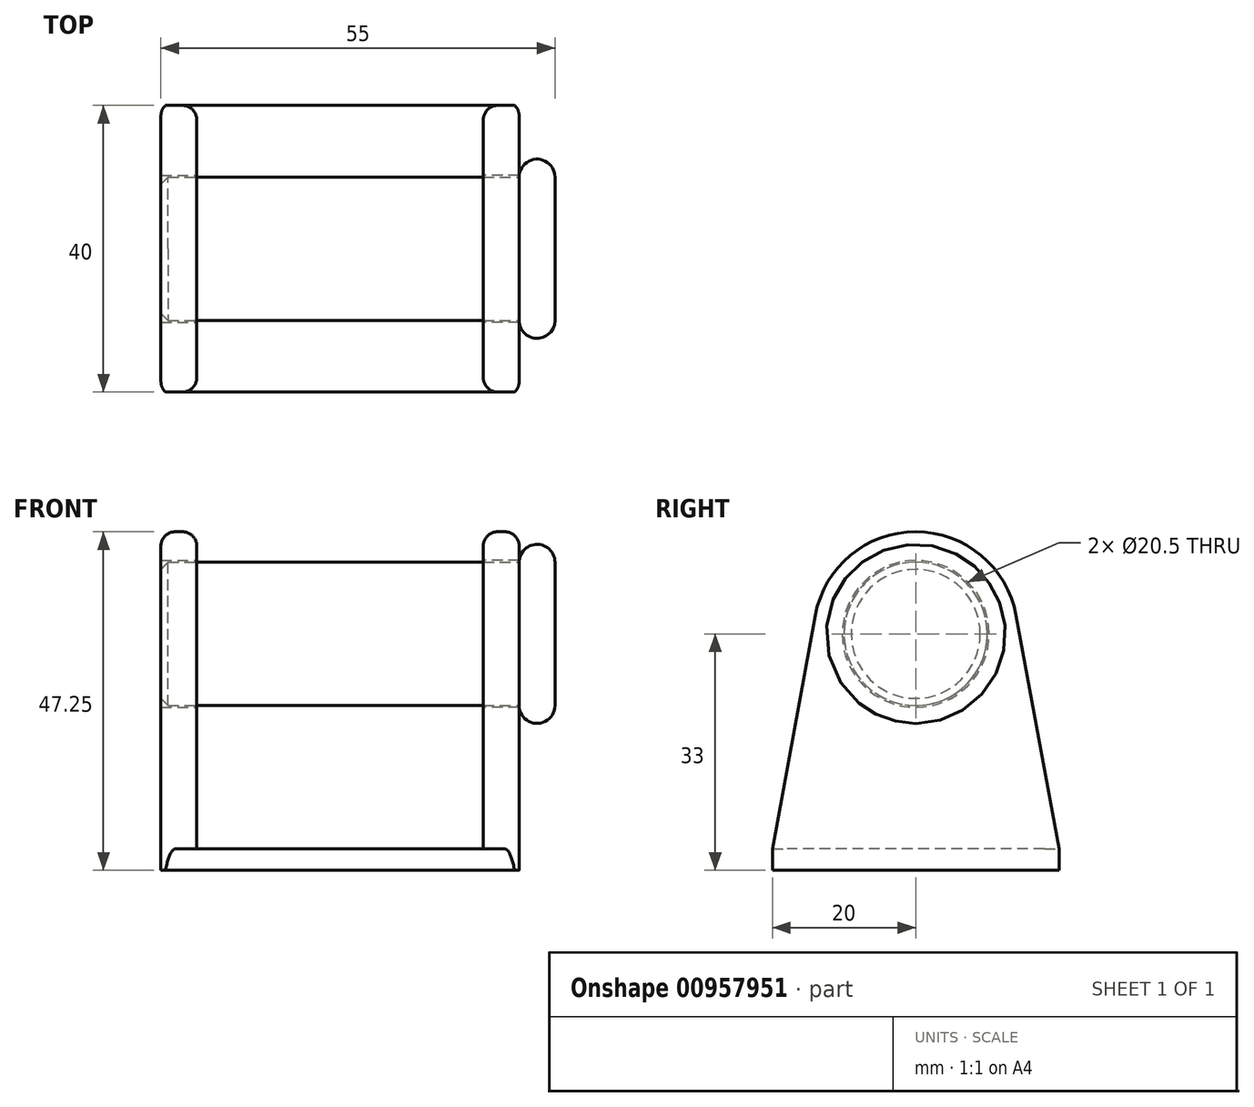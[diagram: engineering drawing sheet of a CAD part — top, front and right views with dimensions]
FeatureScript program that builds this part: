
annotation { "Feature Type Name" : "Feature", "Feature Type Description" : "" }
export const myFeature = defineFeature(function(context is Context, id is Id, definition is map)
    precondition{}
    {
        {
            var Q0;
            Q0=qCreatedBy(makeId("Top.planeOp"),FACE);
            var sketch = newSketch(context, id + "F0", { "sketchPlane" : qUnion([Q0])});
            skLineSegment(sketch, "E0.bottom", {"start": v(25, 20) * mm, "end": v(-25, 20) * mm});
            skLineSegment(sketch, "E0.top", {"start": v(25, -20) * mm, "end": v(-25, -20) * mm});
            skLineSegment(sketch, "E0.left", {"start": v(25, 20) * mm, "end": v(25, -20) * mm});
            skLineSegment(sketch, "E0.right", {"start": v(-25, 20) * mm, "end": v(-25, -20) * mm});
            skPoint(sketch, "E0.middle", {"position": v(0, 0) * mm});
            skLineSegment(sketch, "E1.bottom", {"start": v(20, 20) * mm, "end": v(-20, 20) * mm});
            skLineSegment(sketch, "E1.top", {"start": v(20, -20) * mm, "end": v(-20, -20) * mm});
            skLineSegment(sketch, "E1.left", {"start": v(20, 20) * mm, "end": v(20, -20) * mm});
            skLineSegment(sketch, "E1.right", {"start": v(-20, 20) * mm, "end": v(-20, -20) * mm});
            skSolve(sketch);
        }
        {
            var Q0;
            {var subQ0=sQuery(id+"F0.wireOp",EDGE,"E1.left");Q0=makeQuery(id+"F0.imprint","IMPRINT",FACE,{"disambiguationData":[TD([[makeQuery(id+"F0.imprint","IMPRINT",EDGE,{"derivedFrom":subQ0}),-1.0]])]});}
            var Q1;
            {var subQ0=sQuery(id+"F0.wireOp",EDGE,"E0.right");Q1=makeQuery(id+"F0.imprint","IMPRINT",FACE,{"disambiguationData":[TD([[makeQuery(id+"F0.imprint","IMPRINT",EDGE,{"derivedFrom":subQ0}),1.0]])]});}
            var Q2;
            {var subQ2=sQuery(id+"F0.wireOp",EDGE,"E0.left");Q2=makeQuery(id+"F0.imprint","IMPRINT",FACE,{"disambiguationData":[TD([[makeQuery(id+"F0.imprint","IMPRINT",EDGE,{"derivedFrom":subQ2}),-1.0]])]});}
            extrude(context, id + "F1", {"entities" : qUnion([Q0, Q1, Q2]), "depth" : 3 * mm, "offsetDistance" : 25 * mm});
        }
        {
            var Q0;
            Q0=qCreatedBy(makeId("Right.planeOp"),FACE);
            var sketch = newSketch(context, id + "F2", { "sketchPlane" : qUnion([Q0])});
            skCircle(sketch, "E2", {"center": v(0, 33) * mm, "radius": 10.25 * mm});
            skCircle(sketch, "E3", {"center": v(0, 33) * mm, "radius": 14.25 * mm});
            skLineSegment(sketch, "E4.0", {"start": v(20, 3) * mm, "end": v(-20, 3) * mm});
            skLineSegment(sketch, "E5", {"start": v(-20, 3) * mm, "end": v(-14.02, 35.57) * mm});
            skLineSegment(sketch, "E6", {"start": v(20, 3) * mm, "end": v(14.02, 35.57) * mm});
            skSolve(sketch);
        }
        {
            var Q0;
            Q0=makeQuery(id+"F2.imprint","IMPRINT",FACE,{"disambiguationData":[TD([[makeQuery(id+"F2.imprint","IMPRINT",EDGE,{"derivedFrom":sQuery(id+"F2.wireOp",EDGE,"E4.0")}),-1.0]])]});
            var Q1;
            Q1=makeQuery(id+"F2.imprint","IMPRINT",FACE,{"disambiguationData":[TD([[makeQuery(id+"F2.imprint","IMPRINT",EDGE,{"derivedFrom":sQuery(id+"F2.wireOp",EDGE,"E2")}),-1.0]])]});
            extrude(context, id + "F3", {"entities" : qUnion([Q0, Q1]), "operationType" : NewBodyOperationType.ADD, "depth" : 25 * mm, "offsetDistance" : 25 * mm, "hasSecondDirection" : true, "secondDirectionOppositeDirection" : false, "secondDirectionDepth" : 20 * mm});
        }
        {
            var Q0;
            Q0=makeQuery(id+"F2.imprint","IMPRINT",FACE,{"disambiguationData":[TD([[makeQuery(id+"F2.imprint","IMPRINT",EDGE,{"derivedFrom":sQuery(id+"F2.wireOp",EDGE,"E4.0")}),-1.0]])]});
            var Q1;
            Q1=makeQuery(id+"F2.imprint","IMPRINT",FACE,{"disambiguationData":[TD([[makeQuery(id+"F2.imprint","IMPRINT",EDGE,{"derivedFrom":sQuery(id+"F2.wireOp",EDGE,"E2")}),-1.0]])]});
            extrude(context, id + "F4", {"entities" : qUnion([Q0, Q1]), "operationType" : NewBodyOperationType.ADD, "oppositeDirection" : true, "depth" : 25 * mm, "offsetDistance" : 25 * mm, "hasSecondDirection" : true, "secondDirectionOppositeDirection" : true, "secondDirectionDepth" : 20 * mm});
        }
        {
            var Q0;
            Q0=qCreatedBy(makeId("Front.planeOp"),FACE);
            var sketch = newSketch(context, id + "F5", { "sketchPlane" : qUnion([Q0])});
            skPoint(sketch, "E7.0", {"position": v(0, 33) * mm});
            skLineSegment(sketch, "E8.bottom", {"start": v(25, 23) * mm, "end": v(-25, 23) * mm});
            skLineSegment(sketch, "E8.top", {"start": v(25, 43) * mm, "end": v(-25, 43) * mm});
            skLineSegment(sketch, "E8.left", {"start": v(25, 23) * mm, "end": v(25, 43) * mm});
            skLineSegment(sketch, "E8.right", {"start": v(-25, 23) * mm, "end": v(-25, 43) * mm});
            skLineSegment(sketch, "E9", {"start": v(25, 33) * mm, "end": v(-25, 33) * mm});
            skLineSegment(sketch, "E10.bottom", {"start": v(25, 45.5) * mm, "end": v(30, 45.5) * mm});
            skLineSegment(sketch, "E10.top", {"start": v(25, 20.5) * mm, "end": v(30, 20.5) * mm});
            skLineSegment(sketch, "E10.left", {"start": v(25, 45.5) * mm, "end": v(25, 20.5) * mm});
            skLineSegment(sketch, "E10.right", {"start": v(30, 45.5) * mm, "end": v(30, 20.5) * mm});
            skPoint(sketch, "E10.middle", {"position": v(27.5, 33) * mm});
            skLineSegment(sketch, "E11", {"start": v(25, 33) * mm, "end": v(30, 33) * mm});
            skSolve(sketch);
        }
        {
            var Q0;
            {var subQ0=sQuery(id+"F5.wireOp",EDGE,"E8.bottom");Q0=makeQuery(id+"F5.imprint","IMPRINT",FACE,{"disambiguationData":[TD([[makeQuery(id+"F5.imprint","IMPRINT",EDGE,{"derivedFrom":subQ0}),-1.0]])]});}
            var Q1;
            {var subQ1=sQuery(id+"F5.wireOp",EDGE,"E10.top");Q1=makeQuery(id+"F5.imprint","IMPRINT",FACE,{"disambiguationData":[TD([[makeQuery(id+"F5.imprint","IMPRINT",EDGE,{"derivedFrom":subQ1}),1.0]])]});}
            var Q2;
            Q2=sQuery(id+"F5.wireOp",EDGE,"E9");
            revolve(context, id + "F6", {"surfaceOperationType" : NewSurfaceOperationType.NEW, "entities" : qUnion([Q0, Q1]), "axis" : qUnion([Q2]), "revolveType" : RevolveType.FULL});
        }
        {
            var Q0;
            Q0=makeQuery(id+"F4.opExtrude","CAP_EDGE",EDGE,{"disambiguationData":[OSD([sQuery(id+"F2.wireOp",EDGE,"E6")])],"isStart":true});
            var Q1;
            Q1=makeQuery(id+"F4.opExtrude","CAP_EDGE",EDGE,{"disambiguationData":[OSD([sQuery(id+"F2.wireOp",EDGE,"E6")])],"isStart":false});
            var Q2;
            Q2=makeQuery(id+"F3.opExtrude","CAP_EDGE",EDGE,{"disambiguationData":[OSD([sQuery(id+"F2.wireOp",EDGE,"E6")])],"isStart":true});
            var Q3;
            Q3=makeQuery(id+"F3.opExtrude","CAP_EDGE",EDGE,{"disambiguationData":[OSD([sQuery(id+"F2.wireOp",EDGE,"E6")])],"isStart":false});
            fillet(context, id + "F7", {"entities" : qUnion([Q0, Q1, Q2, Q3]), "radius" : 2 * mm, "tangentPropagation" : true, "allowEdgeOverflow" : false});
        }
        {
            var Q0;
            Q0=makeQuery(id+"F6.opRevolve","SWEPT_EDGE",EDGE,{"disambiguationData":[OSD([sQuery(id+"F5.wireOp",EDGE,"E10.top"),sQuery(id+"F5.wireOp",EDGE,"E10.right")])]});
            var Q1;
            Q1=makeQuery(id+"F6.opRevolve","SWEPT_EDGE",EDGE,{"disambiguationData":[OSD([sQuery(id+"F5.wireOp",EDGE,"E10.top"),sQuery(id+"F5.wireOp",EDGE,"E10.left")])]});
            fillet(context, id + "F8", {"entities" : qUnion([Q0, Q1]), "radius" : 2.5 * mm, "tangentPropagation" : true, "allowEdgeOverflow" : false});
        }
        {
            var Q0;
            Q0=makeQuery(id+"F6.opRevolve","SWEPT_EDGE",EDGE,{"disambiguationData":[OSD([sQuery(id+"F5.wireOp",EDGE,"E8.bottom"),sQuery(id+"F5.wireOp",EDGE,"E8.right")])]});
            chamfer(context, id + "F9", {"entities" : qUnion([Q0]), "width" : 1 * mm, "tangentPropagation" : true});
        }
    });
